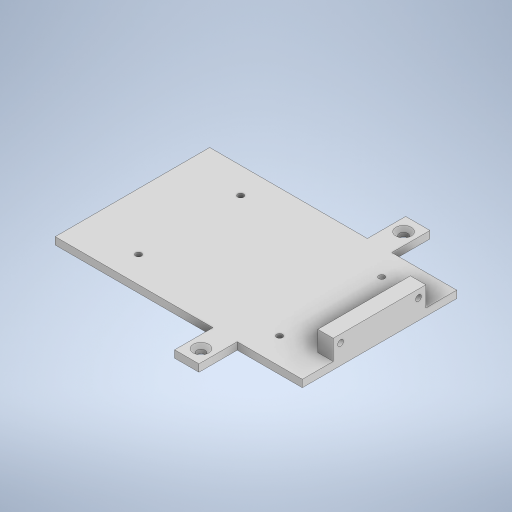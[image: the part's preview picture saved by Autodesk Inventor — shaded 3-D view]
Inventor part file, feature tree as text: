
AUTODESK INVENTOR PART (.ipt)
format: ipt  version: 2024.1 (Build 281209000, 209)  size: 296,448 bytes
history: native  units: in
note: dims shown in document units (in); Inventor stores cm internally (conversion verified against a paired STEP export)
features: sketch x5, hole x3, extrude x2
ambient origin geometry x8: Origin, YZ Plane, XZ Plane, XY Plane, X Axis, Y Axis, Z Axis, Center Point
bodies: Solid1 (feature_tree)
feature tree (10):
  extrude  "Extrusion1"  Depth=3.7402in
  hole  "Hole1"  [1 undecoded]
  extrude  "Extrusion2"  Depth=2.5in
  hole  "Hole2"  [1 undecoded]
  hole  "Hole3"  [1 undecoded]
  sketch  "Sketch1"  dims[d0=0.3937in d1=3.7402in]
  sketch  "Sketch2"  dims[d2=0.1181in d3=0.0in d4=1.6398in]
  sketch  "Sketch3"  dims[d5=1.6398in]
  sketch  "Sketch4"  dims[d6=0.134in d7=0.75in d8=0.248in d9=0.25in d10=90.0deg d11=1.0in d12=0.8108in d13=2.5in]
  sketch  "Sketch5"  dims[d14=2.5in d15=1.5in d16=0.125in d17=1.5in d18=0.325in d19=0.0in d20=0.125in d21=0.6299in d22=1.2598in d23=0.094in d24=0.75in d25=0.173in d26=0.141in d27=90.0deg d28=1.0in d29=0.8108in d30=0.9646in d31=1.9291in d32=3.3465in d33=0.1378in d34=0.1378in d35=0.1378in d36=0.1378in d37=2.2835in d38=180.0deg d39=2.2835in d40=0.094in d41=0.75in d42=0.375in d43=0.25in d44=0.5635in d45=1.0in d46=0.8108in]
note: 3 required parameter values undecoded (feature->parameter linkage not recoverable at this tier; creation-order binding heuristic only, values carry confidence <= 0.55)
